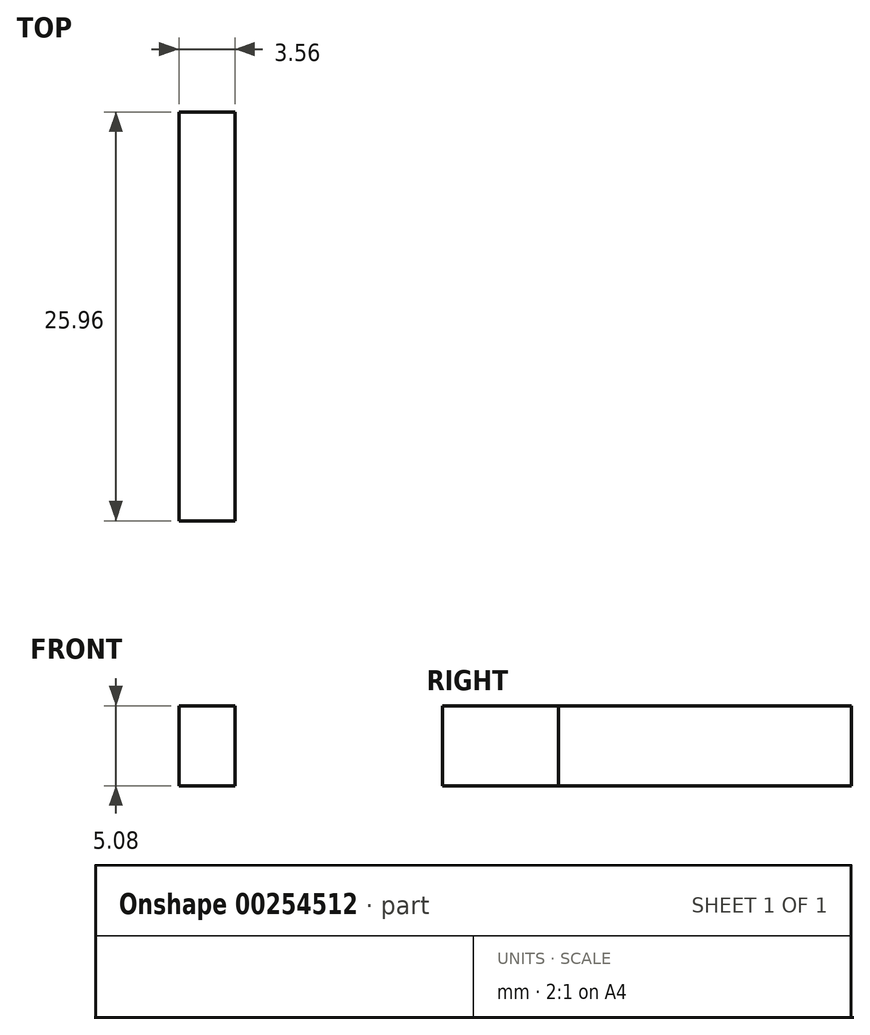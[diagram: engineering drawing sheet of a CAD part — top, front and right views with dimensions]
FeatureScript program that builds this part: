
annotation { "Feature Type Name" : "Feature", "Feature Type Description" : "" }
export const myFeature = defineFeature(function(context is Context, id is Id, definition is map)
    precondition{}
    {
        {
            var Q0;
            Q0=qCreatedBy(makeId("Top.planeOp"),FACE);
            var sketch = newSketch(context, id + "F0", { "sketchPlane" : qUnion([Q0])});
            skLineSegment(sketch, "E0", {"start": v(-33.45, 9.2) * mm, "end": v(-26.8, 16.12) * mm});
            skLineSegment(sketch, "E1", {"start": v(-26.8, 16.12) * mm, "end": v(-22.17, 16.12) * mm});
            skLineSegment(sketch, "E2", {"start": v(-22.17, 16.12) * mm, "end": v(-22.17, 19.99) * mm});
            skLineSegment(sketch, "E3", {"start": v(-22.17, 19.99) * mm, "end": v(-25.8, 19.97) * mm});
            skLineSegment(sketch, "E4", {"start": v(-25.8, 19.97) * mm, "end": v(-25.8, 38.73) * mm});
            skLineSegment(sketch, "E5", {"start": v(-25.8, 38.73) * mm, "end": v(-18.88, 45.9) * mm});
            skLineSegment(sketch, "E6", {"start": v(-18.88, 45.9) * mm, "end": v(14.3, 45.9) * mm});
            skLineSegment(sketch, "E7", {"start": v(14.3, 45.9) * mm, "end": v(22.2, 38.73) * mm});
            skLineSegment(sketch, "E8", {"start": v(22.2, 38.73) * mm, "end": v(22.2, 19.97) * mm});
            skLineSegment(sketch, "E9", {"start": v(22.2, 19.97) * mm, "end": v(18.52, 19.97) * mm});
            skLineSegment(sketch, "E10", {"start": v(18.52, 19.97) * mm, "end": v(18.52, 16.12) * mm});
            skLineSegment(sketch, "E11", {"start": v(18.52, 16.12) * mm, "end": v(22.2, 16.12) * mm});
            skLineSegment(sketch, "E12", {"start": v(22.2, 16.12) * mm, "end": v(29.83, 9.43) * mm});
            skLineSegment(sketch, "E13", {"start": v(29.83, 9.43) * mm, "end": v(29.83, -20.85) * mm});
            skLineSegment(sketch, "E14", {"start": v(29.83, -20.85) * mm, "end": v(22.14, -20.85) * mm});
            skLineSegment(sketch, "E15", {"start": v(22.14, -20.85) * mm, "end": v(22.14, -32.04) * mm});
            skLineSegment(sketch, "E16", {"start": v(22.14, -32.04) * mm, "end": v(19.03, -35.7) * mm});
            skLineSegment(sketch, "E17", {"start": v(19.03, -35.7) * mm, "end": v(3.87, -35.7) * mm});
            skLineSegment(sketch, "E18", {"start": v(3.87, -35.7) * mm, "end": v(3.87, -28.47) * mm});
            skLineSegment(sketch, "E19", {"start": v(3.87, -28.47) * mm, "end": v(-7.29, -28.47) * mm});
            skLineSegment(sketch, "E20", {"start": v(-7.29, -28.47) * mm, "end": v(-7.29, -35.7) * mm});
            skLineSegment(sketch, "E21", {"start": v(-7.29, -35.7) * mm, "end": v(-23.05, -35.7) * mm});
            skLineSegment(sketch, "E22", {"start": v(-23.05, -35.7) * mm, "end": v(-25.8, -32.44) * mm});
            skLineSegment(sketch, "E23", {"start": v(-25.8, -32.44) * mm, "end": v(-25.8, -20.85) * mm});
            skLineSegment(sketch, "E24", {"start": v(-25.8, -20.85) * mm, "end": v(-33.32, -20.85) * mm});
            skLineSegment(sketch, "E25", {"start": v(-33.32, -20.85) * mm, "end": v(-33.45, 9.2) * mm});
            skCircle(sketch, "E26", {"center": v(-11.3, 31.23) * mm, "radius": 5.9 * mm});
            skPoint(sketch, "E26.first.point", {"position": v(-17.19, 30.94) * mm});
            skPoint(sketch, "E26.second.point", {"position": v(-5.4, 31.07) * mm});
            skPoint(sketch, "E26.third.point", {"position": v(-11.26, 25.33) * mm});
            skCircle(sketch, "E27", {"center": v(7.12, 31) * mm, "radius": 5.64 * mm});
            skPoint(sketch, "E27.first.point", {"position": v(1.48, 30.84) * mm});
            skPoint(sketch, "E27.second.point", {"position": v(12.76, 30.78) * mm});
            skPoint(sketch, "E27.third.point", {"position": v(7.1, 36.64) * mm});
            skLineSegment(sketch, "E28.bottom", {"start": v(-14.96, 34.57) * mm, "end": v(-7.5, 34.57) * mm});
            skLineSegment(sketch, "E28.top", {"start": v(-14.96, 27.44) * mm, "end": v(-7.5, 27.44) * mm});
            skLineSegment(sketch, "E28.left", {"start": v(-14.96, 34.57) * mm, "end": v(-14.96, 27.44) * mm});
            skLineSegment(sketch, "E28.right", {"start": v(-7.5, 34.57) * mm, "end": v(-7.5, 27.44) * mm});
            skLineSegment(sketch, "E29.bottom", {"start": v(3.8, 34.28) * mm, "end": v(10.72, 34.28) * mm});
            skLineSegment(sketch, "E29.top", {"start": v(3.8, 27.44) * mm, "end": v(10.72, 27.44) * mm});
            skLineSegment(sketch, "E29.left", {"start": v(3.8, 34.28) * mm, "end": v(3.8, 27.44) * mm});
            skLineSegment(sketch, "E29.right", {"start": v(10.72, 34.28) * mm, "end": v(10.72, 27.44) * mm});
            skLineSegment(sketch, "E30.bottom", {"start": v(7.12, 31) * mm, "end": v(3.8, 31) * mm});
            skLineSegment(sketch, "E30.top", {"start": v(7.12, 34.28) * mm, "end": v(3.8, 34.28) * mm});
            skLineSegment(sketch, "E30.left", {"start": v(7.12, 31) * mm, "end": v(7.12, 34.28) * mm});
            skLineSegment(sketch, "E30.right", {"start": v(3.8, 31) * mm, "end": v(3.8, 34.28) * mm});
            skLineSegment(sketch, "E31.bottom", {"start": v(-11.3, 31.23) * mm, "end": v(-14.96, 31.23) * mm});
            skLineSegment(sketch, "E31.top", {"start": v(-11.3, 34.57) * mm, "end": v(-14.96, 34.57) * mm});
            skLineSegment(sketch, "E31.left", {"start": v(-11.3, 31.23) * mm, "end": v(-11.3, 34.57) * mm});
            skLineSegment(sketch, "E31.right", {"start": v(-14.96, 31.23) * mm, "end": v(-14.96, 34.57) * mm});
            skLineSegment(sketch, "E32.bottom", {"start": v(-3.8, 23.6) * mm, "end": v(0, 23.6) * mm});
            skLineSegment(sketch, "E32.top", {"start": v(-3.8, 19.8) * mm, "end": v(0, 19.8) * mm});
            skLineSegment(sketch, "E32.left", {"start": v(-3.8, 23.6) * mm, "end": v(-3.8, 19.8) * mm});
            skLineSegment(sketch, "E32.right", {"start": v(0, 23.6) * mm, "end": v(0, 19.8) * mm});
            skLineSegment(sketch, "E33.bottom", {"start": v(-7.5, 15.86) * mm, "end": v(3.8, 15.86) * mm});
            skLineSegment(sketch, "E33.top", {"start": v(-7.5, 12.27) * mm, "end": v(3.8, 12.27) * mm});
            skLineSegment(sketch, "E33.left", {"start": v(-7.5, 15.86) * mm, "end": v(-7.5, 12.27) * mm});
            skLineSegment(sketch, "E33.right", {"start": v(3.8, 15.86) * mm, "end": v(3.8, 12.27) * mm});
            skPoint(sketch, "E34.oppositeSnap0", {"position": v(-25.8, -26.64) * mm});
            skLineSegment(sketch, "E34.bottom", {"start": v(-29.45, -9.9) * mm, "end": v(-25.8, -9.9) * mm});
            skLineSegment(sketch, "E34.top", {"start": v(-29.45, -17.27) * mm, "end": v(-25.8, -17.27) * mm});
            skLineSegment(sketch, "E34.left", {"start": v(-29.45, -9.9) * mm, "end": v(-29.45, -17.27) * mm});
            skLineSegment(sketch, "E34.right", {"start": v(-25.8, -9.9) * mm, "end": v(-25.8, -17.27) * mm});
            skLineSegment(sketch, "E35.top", {"start": v(-29.45, 8.74) * mm, "end": v(-25.8, 8.74) * mm});
            skLineSegment(sketch, "E35.left", {"start": v(-29.45, -9.9) * mm, "end": v(-29.45, 8.74) * mm});
            skLineSegment(sketch, "E35.right", {"start": v(-25.8, -9.9) * mm, "end": v(-25.8, 8.74) * mm});
            skLineSegment(sketch, "E36.bottom", {"start": v(22.2, -9.9) * mm, "end": v(25.76, -9.9) * mm});
            skLineSegment(sketch, "E36.top", {"start": v(22.2, -17.27) * mm, "end": v(25.76, -17.27) * mm});
            skLineSegment(sketch, "E36.left", {"start": v(22.2, -9.9) * mm, "end": v(22.2, -17.27) * mm});
            skLineSegment(sketch, "E36.right", {"start": v(25.76, -9.9) * mm, "end": v(25.76, -17.27) * mm});
            skLineSegment(sketch, "E37.top", {"start": v(22.2, 8.7) * mm, "end": v(25.76, 8.7) * mm});
            skLineSegment(sketch, "E37.left", {"start": v(22.2, -9.9) * mm, "end": v(22.2, 8.7) * mm});
            skLineSegment(sketch, "E37.right", {"start": v(25.76, -9.9) * mm, "end": v(25.76, 8.7) * mm});
            skLineSegment(sketch, "E38.bottom", {"start": v(-3.6, -28.47) * mm, "end": v(0, -28.47) * mm});
            skLineSegment(sketch, "E38.top", {"start": v(-3.6, -24.74) * mm, "end": v(0, -24.74) * mm});
            skLineSegment(sketch, "E38.left", {"start": v(-3.6, -28.47) * mm, "end": v(-3.6, -24.74) * mm});
            skLineSegment(sketch, "E38.right", {"start": v(0, -28.47) * mm, "end": v(0, -24.74) * mm});
            skLineSegment(sketch, "E39", {"start": v(-22.24, -24.61) * mm, "end": v(-22.24, -31.85) * mm});
            skLineSegment(sketch, "E40", {"start": v(-22.24, -31.85) * mm, "end": v(-11.06, -31.85) * mm});
            skLineSegment(sketch, "E41", {"start": v(-11.06, -31.85) * mm, "end": v(-11.06, -28.48) * mm});
            skLineSegment(sketch, "E42", {"start": v(-11.06, -28.48) * mm, "end": v(-7.29, -28.47) * mm});
            skLineSegment(sketch, "E43", {"start": v(-7.29, -24.61) * mm, "end": v(-22.24, -24.61) * mm});
            skLineSegment(sketch, "E44", {"start": v(-7.29, -24.61) * mm, "end": v(-7.29, -28.47) * mm});
            skLineSegment(sketch, "E45", {"start": v(3.87, -28.47) * mm, "end": v(3.87, -24.61) * mm});
            skLineSegment(sketch, "E46", {"start": v(3.87, -24.61) * mm, "end": v(18.56, -24.61) * mm});
            skLineSegment(sketch, "E47", {"start": v(18.56, -24.61) * mm, "end": v(18.56, -31.97) * mm});
            skLineSegment(sketch, "E48", {"start": v(18.56, -31.97) * mm, "end": v(7.4, -31.97) * mm});
            skLineSegment(sketch, "E49", {"start": v(7.4, -31.97) * mm, "end": v(7.4, -28.47) * mm});
            skLineSegment(sketch, "E50", {"start": v(7.4, -28.47) * mm, "end": v(3.87, -28.47) * mm});
            skLineSegment(sketch, "E51", {"start": v(-22.17, 19.99) * mm, "end": v(-22.24, 38.23) * mm});
            skLineSegment(sketch, "E52", {"start": v(-22.24, 38.23) * mm, "end": v(-18.48, 38.25) * mm});
            skLineSegment(sketch, "E53", {"start": v(-18.48, 38.25) * mm, "end": v(-18.5, 42.04) * mm});
            skLineSegment(sketch, "E54", {"start": v(-18.5, 42.04) * mm, "end": v(14.76, 42.16) * mm});
            skLineSegment(sketch, "E55", {"start": v(14.76, 42.16) * mm, "end": v(14.78, 38.23) * mm});
            skLineSegment(sketch, "E56", {"start": v(14.78, 38.23) * mm, "end": v(18.52, 38.24) * mm});
            skLineSegment(sketch, "E57", {"start": v(18.52, 38.24) * mm, "end": v(18.52, 19.97) * mm});
            skLineSegment(sketch, "E58", {"start": v(3.8, 15.86) * mm, "end": v(3.8, 19.97) * mm});
            skLineSegment(sketch, "E59", {"start": v(3.8, 19.97) * mm, "end": v(18.52, 19.97) * mm});
            skLineSegment(sketch, "E60", {"start": v(-7.5, 15.86) * mm, "end": v(-7.5, 19.99) * mm});
            skLineSegment(sketch, "E61", {"start": v(-7.5, 19.99) * mm, "end": v(-22.17, 19.99) * mm});
            skLineSegment(sketch, "E62", {"start": v(-22.23, 12.38) * mm, "end": v(-22.23, -21.38) * mm});
            skLineSegment(sketch, "E63", {"start": v(-22.23, -21.38) * mm, "end": v(18.48, -21.38) * mm});
            skLineSegment(sketch, "E64", {"start": v(18.48, -21.38) * mm, "end": v(18.48, 12.34) * mm});
            skLineSegment(sketch, "E65", {"start": v(18.48, 12.34) * mm, "end": v(14.65, 12.34) * mm});
            skLineSegment(sketch, "E66", {"start": v(14.65, 12.34) * mm, "end": v(14.65, 15.86) * mm});
            skLineSegment(sketch, "E67", {"start": v(14.65, 15.86) * mm, "end": v(3.8, 15.86) * mm});
            skLineSegment(sketch, "E68", {"start": v(-22.23, 12.38) * mm, "end": v(-18.53, 12.38) * mm});
            skLineSegment(sketch, "E69", {"start": v(-18.53, 12.38) * mm, "end": v(-18.53, 15.86) * mm});
            skLineSegment(sketch, "E70", {"start": v(-18.53, 15.86) * mm, "end": v(-7.5, 15.86) * mm});
            skLineSegment(sketch, "E71.bottom", {"start": v(-7.42, -28.31) * mm, "end": v(-7.13, -28.31) * mm});
            skLineSegment(sketch, "E71.top", {"start": v(-7.42, -28.63) * mm, "end": v(-7.13, -28.63) * mm});
            skLineSegment(sketch, "E71.left", {"start": v(-7.42, -28.31) * mm, "end": v(-7.42, -28.63) * mm});
            skLineSegment(sketch, "E71.right", {"start": v(-7.13, -28.31) * mm, "end": v(-7.13, -28.63) * mm});
            skLineSegment(sketch, "E72.bottom", {"start": v(3.95, -28.38) * mm, "end": v(3.78, -28.38) * mm});
            skLineSegment(sketch, "E72.top", {"start": v(3.95, -28.56) * mm, "end": v(3.78, -28.56) * mm});
            skLineSegment(sketch, "E72.left", {"start": v(3.95, -28.38) * mm, "end": v(3.95, -28.56) * mm});
            skLineSegment(sketch, "E72.right", {"start": v(3.78, -28.38) * mm, "end": v(3.78, -28.56) * mm});
            skSolve(sketch);
        }
        {
            var Q0;
            Q0=makeQuery(id+"F0.imprint","IMPRINT",FACE,{"disambiguationData":[TD([[makeQuery(id+"F0.imprint","IMPRINT",EDGE,{"derivedFrom":sQuery(id+"F0.wireOp",EDGE,"E37.top")}),-1.0]])]});
            var Q1;
            Q1=makeQuery(id+"F0.imprint","IMPRINT",FACE,{"disambiguationData":[TD([[makeQuery(id+"F0.imprint","IMPRINT",EDGE,{"derivedFrom":sQuery(id+"F0.wireOp",EDGE,"E36.top")}),1.0]])]});
            extrude(context, id + "F1", {"entities" : qUnion([Q0, Q1]), "depth" : 5.08 * mm});
        }
    });
